# Revit family: Haworth_GranTorino_Armchair
name_source: partatom
category: Furniture
revit_build: Autodesk Revit 2018 (Build: 20170223_1515(x64)
units: mm (PartAtom-declared; Revit-internal decimal feet)

## family parameters
Always vertical = Yes
Cut with Voids When Loaded = No
OmniClass Number = 23.40.20.00
OmniClass Title = General Furniture and Specialties
Room Calculation Point = No
Shared = No
Work Plane-Based = No

## types (1)
- HCPF-GHL1
    Actual Depth = 2' - 10 1/4"
    Actual Height = 4' - 1 11/16"
    Actual Width = 3' - 9"
    Assembly Code = E2020200
    Description = Haworth GranTorino HB Large Armchair
    Leg Finish = Haworth _ Metal _ Brushed Aluminum
    Manufacturer = Haworth
    Model = HCPF-GHL1
    Size = Verify Final Dim. w/ Haworth
    URL = http://www.haworth.com
    URL - Product = http://www.haworth.com
    Version = 3
    Warranty = http://www.haworth.com

## geometry (parser evidence)
native form markers: Blend x8, Sweep x17
no freeform markers — native parametric forms only
